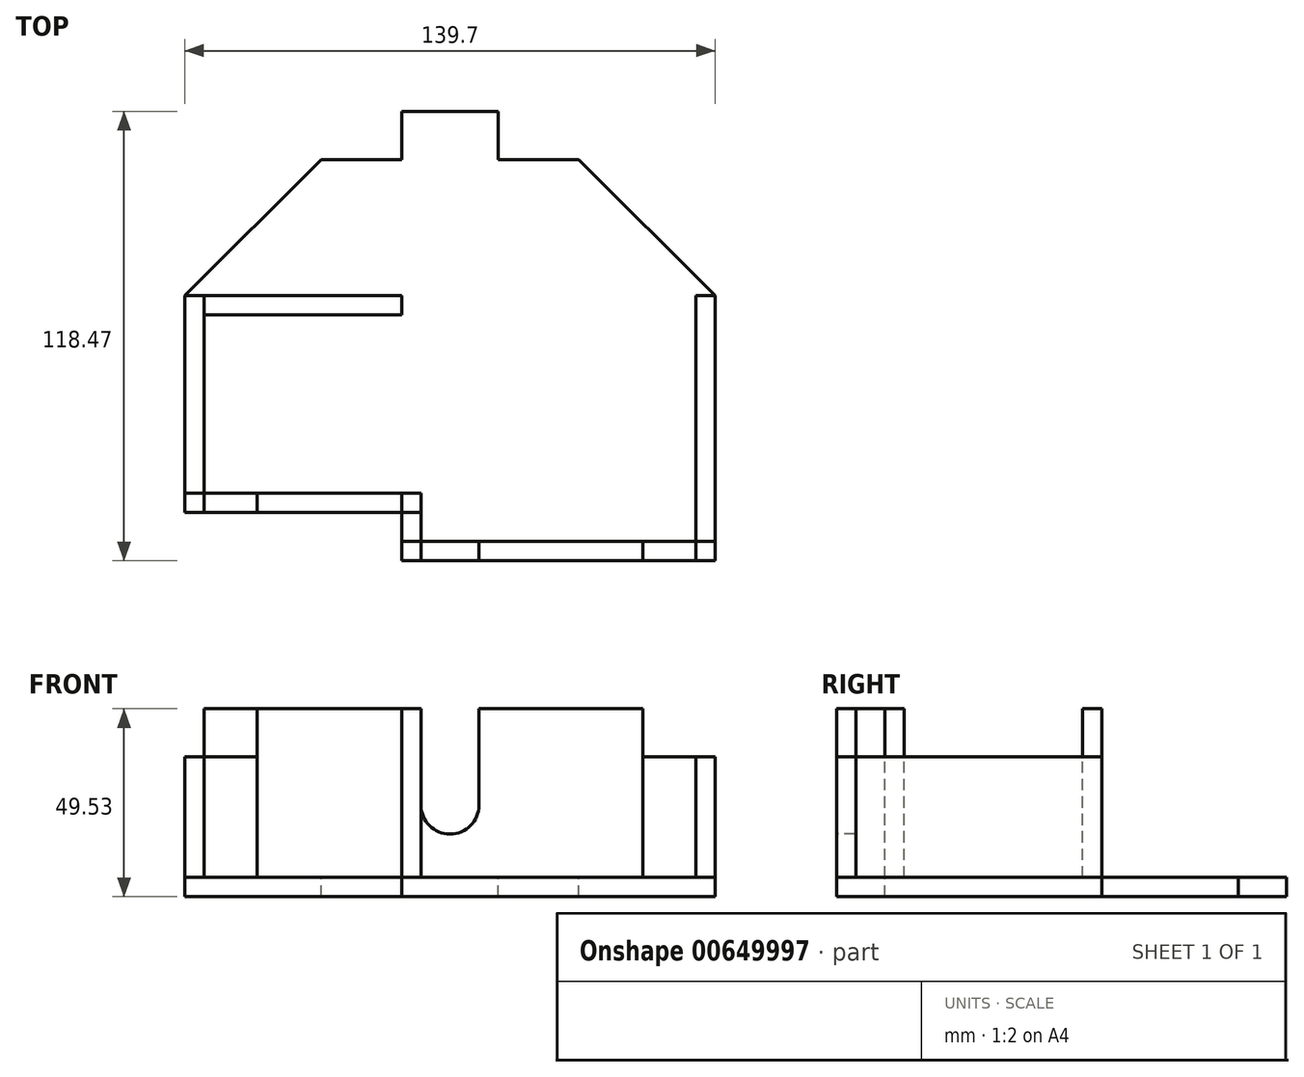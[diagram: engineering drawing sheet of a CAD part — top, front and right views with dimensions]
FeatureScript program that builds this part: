
annotation { "Feature Type Name" : "Feature", "Feature Type Description" : "" }
export const myFeature = defineFeature(function(context is Context, id is Id, definition is map)
    precondition{}
    {
        {
            var Q0;
            Q0=qCreatedBy(makeId("Top.planeOp"),FACE);
            var sketch = newSketch(context, id + "F0", { "sketchPlane" : qUnion([Q0])});
            skLineSegment(sketch, "E0.top", {"start": v(0, 57.15) * mm, "end": v(5.08, 57.15) * mm});
            skLineSegment(sketch, "E0.left", {"start": v(0, 0) * mm, "end": v(0, 57.15) * mm});
            skLineSegment(sketch, "E0.right", {"start": v(139.7, 0) * mm, "end": v(139.7, 57.15) * mm});
            skLineSegment(sketch, "E1.bottom", {"start": v(69.85, 57.15) * mm, "end": v(103.78, 57.15) * mm});
            skLineSegment(sketch, "E1.top", {"start": v(82.55, 93.07) * mm, "end": v(103.78, 93.07) * mm});
            skLineSegment(sketch, "E1.left", {"start": v(69.85, 57.15) * mm, "end": v(69.85, 93.07) * mm});
            skLineSegment(sketch, "E1.right", {"start": v(103.78, 57.15) * mm, "end": v(103.78, 93.07) * mm});
            skLineSegment(sketch, "E2", {"start": v(103.78, 93.07) * mm, "end": v(139.7, 57.15) * mm});
            skLineSegment(sketch, "E3", {"start": v(69.85, 93.07) * mm, "end": v(69.85, 0) * mm});
            skLineSegment(sketch, "E4.MirrorCS", {"start": v(35.92, 93.07) * mm, "end": v(0, 57.15) * mm});
            skLineSegment(sketch, "E5.MirrorCS", {"start": v(57.15, 93.07) * mm, "end": v(35.92, 93.07) * mm});
            skLineSegment(sketch, "E6.bottom", {"start": v(139.7, 0) * mm, "end": v(69.85, 0) * mm});
            skLineSegment(sketch, "E6.top", {"start": v(139.7, -12.7) * mm, "end": v(120.65, -12.7) * mm});
            skLineSegment(sketch, "E6.left", {"start": v(139.7, 0) * mm, "end": v(139.7, -12.7) * mm});
            skLineSegment(sketch, "E6.right", {"start": v(57.15, 0) * mm, "end": v(57.15, -12.7) * mm});
            skLineSegment(sketch, "E7.top", {"start": v(69.85, 105.77) * mm, "end": v(82.55, 105.77) * mm});
            skLineSegment(sketch, "E7.left", {"start": v(69.85, 93.07) * mm, "end": v(69.85, 105.77) * mm});
            skLineSegment(sketch, "E7.right", {"start": v(82.55, 93.07) * mm, "end": v(82.55, 105.77) * mm});
            skLineSegment(sketch, "E8.MirrorCS", {"start": v(57.15, 93.07) * mm, "end": v(57.15, 105.77) * mm});
            skLineSegment(sketch, "E9.MirrorCS", {"start": v(69.85, 105.77) * mm, "end": v(57.15, 105.77) * mm});
            skLineSegment(sketch, "E10.trimOffspring", {"start": v(69.85, 0) * mm, "end": v(139.7, 0) * mm});
            skPoint(sketch, "E11.orphan", {"position": v(69.85, 93.07) * mm});
            skLineSegment(sketch, "E12", {"start": v(69.85, 57.15) * mm, "end": v(139.7, 57.15) * mm});
            skLineSegment(sketch, "E13", {"start": v(120.65, -12.7) * mm, "end": v(82.55, -12.7) * mm});
            skLineSegment(sketch, "E14", {"start": v(82.55, -12.7) * mm, "end": v(57.15, -12.7) * mm});
            skLineSegment(sketch, "E15", {"start": v(19.05, 0) * mm, "end": v(19.05, 0) * mm});
            skLineSegment(sketch, "E16", {"start": v(0, 0) * mm, "end": v(19.05, 0) * mm});
            skLineSegment(sketch, "E17", {"start": v(19.05, 0) * mm, "end": v(57.15, 0) * mm});
            skLineSegment(sketch, "E18", {"start": v(57.15, 57.15) * mm, "end": v(69.85, 57.15) * mm});
            skLineSegment(sketch, "E19", {"start": v(5.08, 57.15) * mm, "end": v(57.15, 57.15) * mm});
            skSolve(sketch);
        }
        {
            var Q0;
            Q0 = qSketchRegion(id + "F0", true);
            var Q1;
            Q1=sQuery(id+"F0.wireOp",EDGE,"E0.left");
            var Q2;
            Q2=sQuery(id+"F0.wireOp",EDGE,"E16");
            var Q3;
            Q3=sQuery(id+"F0.wireOp",EDGE,"E6.top");
            var Q4;
            Q4=sQuery(id+"F0.wireOp",EDGE,"E6.left");
            var Q5;
            Q5=sQuery(id+"F0.wireOp",EDGE,"E0.right");
            extrude(context, id + "F1", {"entities" : qUnion([Q0]), "bodyType" : ToolBodyType.SURFACE, "surfaceEntities" : qUnion([Q1, Q2, Q3, Q4, Q5]), "depth" : 31.75 * mm, "offsetDistance" : 25.4 * mm});
        }
        {
            var Q0;
            Q0 = qSketchRegion(id + "F0", true);
            var Q1;
            Q1=sQuery(id+"F0.wireOp",EDGE,"E19");
            var Q2;
            Q2=sQuery(id+"F0.wireOp",EDGE,"E17");
            var Q3;
            Q3=sQuery(id+"F0.wireOp",EDGE,"E6.right");
            var Q4;
            Q4=sQuery(id+"F0.wireOp",EDGE,"E14");
            var Q5;
            Q5=sQuery(id+"F0.wireOp",EDGE,"E13");
            extrude(context, id + "F2", {"entities" : qUnion([Q0]), "bodyType" : ToolBodyType.SURFACE, "surfaceEntities" : qUnion([Q1, Q2, Q3, Q4, Q5]), "depth" : 44.45 * mm, "offsetDistance" : 25.4 * mm});
        }
        {
            var Q0;
            Q0=makeQuery(id+"F1.opExtrude","SWEPT_FACE",FACE,{"disambiguationData":[OSD([sQuery(id+"F0.wireOp",EDGE,"E0.right"),sQuery(id+"F0.wireOp",EDGE,"E6.left")])]});
            extrude(context, id + "F3", {"entities" : qUnion([Q0]), "depth" : 5.08 * mm, "offsetDistance" : 25.4 * mm});
        }
        {
            var Q0;
            Q0=makeQuery(id+"F1.opExtrude","SWEPT_FACE",FACE,{"disambiguationData":[OSD([sQuery(id+"F0.wireOp",EDGE,"E16")])]});
            var Q1;
            Q1=makeQuery(id+"FyYz8MLdxKTTn0Z_2.opExtrude","SWEPT_FACE",FACE,{"disambiguationData":[OSD([sQuery(id+"F0.wireOp",EDGE,"E17")])]});
            var Q2;
            Q2=makeQuery(id+"FyYz8MLdxKTTn0Z_2.opExtrude","SWEPT_FACE",FACE,{"disambiguationData":[OSD([sQuery(id+"F0.wireOp",EDGE,"E13"),sQuery(id+"F0.wireOp",EDGE,"E14")])]});
            var Q3;
            Q3=makeQuery(id+"F1.opExtrude","SWEPT_FACE",FACE,{"disambiguationData":[OSD([sQuery(id+"F0.wireOp",EDGE,"E6.top")])]});
            extrude(context, id + "F4", {"entities" : qUnion([Q0, Q1, Q2, Q3]), "depth" : 5.08 * mm, "offsetDistance" : 25.4 * mm});
        }
        {
            var Q0;
            Q0=makeQuery(id+"F1.opExtrude","SWEPT_FACE",FACE,{"disambiguationData":[OSD([sQuery(id+"F0.wireOp",EDGE,"E0.left")])]});
            extrude(context, id + "F5", {"entities" : qUnion([Q0]), "depth" : 5.08 * mm, "offsetDistance" : 25.4 * mm});
        }
        {
            var Q0;
            Q0=makeQuery(id+"F2.opExtrude","SWEPT_FACE",FACE,{"disambiguationData":[OSD([sQuery(id+"F0.wireOp",EDGE,"E19")])]});
            extrude(context, id + "F6", {"entities" : qUnion([Q0]), "operationType" : NewBodyOperationType.ADD, "depth" : 5.08 * mm, "offsetDistance" : 25.4 * mm});
        }
        {
            var Q0;
            Q0=makeQuery(id+"F2.opExtrude","SWEPT_FACE",FACE,{"disambiguationData":[OSD([sQuery(id+"F0.wireOp",EDGE,"E13"),sQuery(id+"F0.wireOp",EDGE,"E14")])]});
            var sketch = newSketch(context, id + "F7", { "sketchPlane" : qUnion([Q0])});
            skLineSegment(sketch, "E20.bottom", {"start": v(62.23, 44.45) * mm, "end": v(77.47, 44.45) * mm});
            skLineSegment(sketch, "E20.top", {"start": v(62.23, 0) * mm, "end": v(77.47, 0) * mm});
            skLineSegment(sketch, "E20.left", {"start": v(62.23, 44.45) * mm, "end": v(62.23, 0) * mm});
            skLineSegment(sketch, "E20.right", {"start": v(77.47, 44.45) * mm, "end": v(77.47, 0) * mm});
            skLineSegment(sketch, "E21.top", {"start": v(69.85, 11.43) * mm, "end": v(69.85, 11.43) * mm});
            skLineSegment(sketch, "E21.left", {"start": v(62.23, 44.45) * mm, "end": v(62.23, 19.05) * mm});
            skLineSegment(sketch, "E21.right", {"start": v(77.47, 44.45) * mm, "end": v(77.47, 19.05) * mm});
            skPoint(sketch, "E22.visualSharp", {"position": v(62.23, 11.43) * mm});
            skArc(sketch, "E22.filletArc", {"start": v(62.23, 19.05) * mm, "mid": v(64.46, 13.66) * mm, "end": v(69.85, 11.43) * mm});
            skPoint(sketch, "E23.visualSharp", {"position": v(77.47, 11.43) * mm});
            skArc(sketch, "E23.filletArc", {"start": v(69.85, 11.43) * mm, "mid": v(75.24, 13.66) * mm, "end": v(77.47, 19.05) * mm});
            skSolve(sketch);
        }
        {
            var Q0;
            {var subQ5=sQuery(id+"F7.wireOp",EDGE,"E20.left");Q0=makeQuery(id+"F7.imprint","IMPRINT",FACE,{"disambiguationData":[TD([[makeQuery(id+"F7.imprint","IMPRINT",EDGE,{"derivedFrom":subQ5}),-1.0]])]});}
            var Q1;
            Q1=makeQuery(id+"F7.imprint","IMPRINT",FACE,{"disambiguationData":[TD([[makeQuery(id+"F7.imprint","IMPRINT",EDGE,{"derivedFrom":sQuery(id+"F7.wireOp",EDGE,"E20.top")}),1.0]])]});
            var Q2;
            {var subQ4=sQuery(id+"F7.wireOp",EDGE,"E20.right");Q2=makeQuery(id+"F7.imprint","IMPRINT",FACE,{"disambiguationData":[TD([[makeQuery(id+"F7.imprint","IMPRINT",EDGE,{"derivedFrom":subQ4}),1.0]])]});}
            var Q3;
            Q3=makeQuery(id+"F2.opExtrude","SWEPT_FACE",FACE,{"disambiguationData":[OSD([sQuery(id+"F0.wireOp",EDGE,"E17")])]});
            extrude(context, id + "F8", {"entities" : qUnion([Q0, Q1, Q2, Q3]), "oppositeDirection" : true, "depth" : 5.08 * mm, "offsetDistance" : 25.4 * mm});
        }
        {
            var Q0;
            Q0=makeQuery(id+"F2.opExtrude","SWEPT_FACE",FACE,{"disambiguationData":[OSD([sQuery(id+"F0.wireOp",EDGE,"E6.right")])]});
            var Q1;
            Q1=makeQuery(id+"F8.opExtrude","SWEPT_FACE",FACE,{"disambiguationData":[OSD([sQuery(id+"F0.wireOp",VERTEX,"E6.right.start")])]});
            extrude(context, id + "F9", {"entities" : qUnion([Q0, Q1]), "oppositeDirection" : true, "depth" : 5.08 * mm, "offsetDistance" : 25.4 * mm});
        }
        {
            var Q0;
            Q0 = qSketchRegion(id + "F0", true);
            extrude(context, id + "F10", {"entities" : qUnion([Q0]), "oppositeDirection" : true, "depth" : 5.08 * mm, "offsetDistance" : 25.4 * mm});
        }
    });
